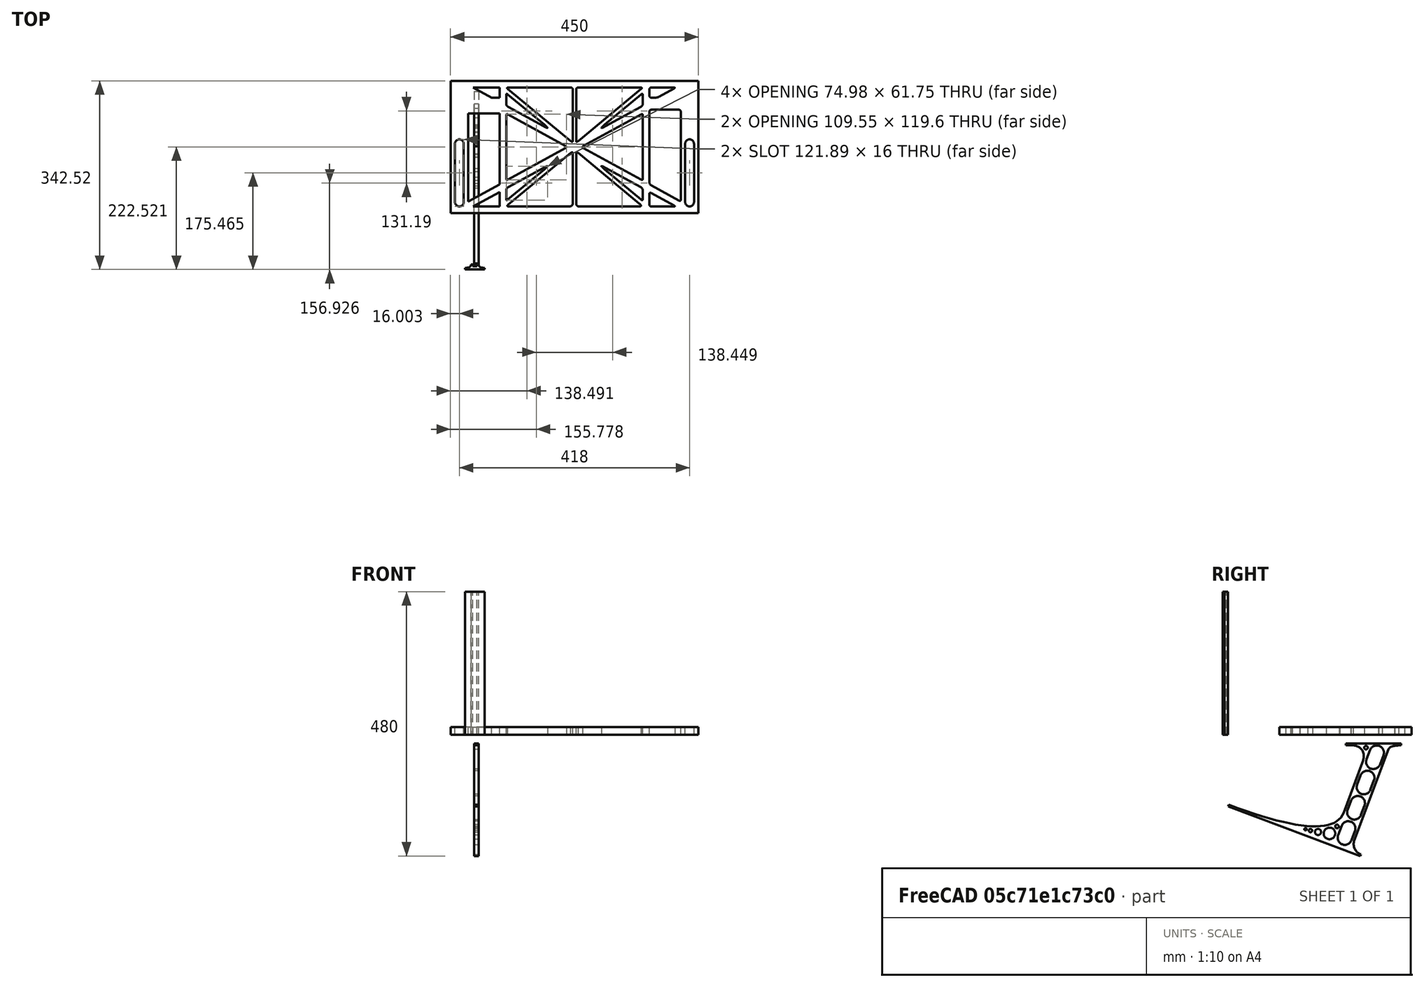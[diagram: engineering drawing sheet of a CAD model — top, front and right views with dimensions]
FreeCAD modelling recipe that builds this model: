
FCSTD DOCUMENT  (FreeCAD 0.19R0.19.2)
Label: laptopStand114
License: All rights reserved
LicenseURL: http://en.wikipedia.org/wiki/All_rights_reserved
objects: Sketcher::SketchObject×3, Part::Extrusion×3
note: 6 computed .brp shape members not serialized (recipe doc carries the construction recipe); baked Part::Feature solids carry a one-line shape summary decoded from their .brp

FEATURE [Sketcher::SketchObject] Sketch
  FullyConstrained = false
  sketch-geometry (318):
    g0: LineSegment StartX=-10.9272 StartY=-82.7794 StartZ=0 EndX=46.0728 EndY=-51.4823 EndZ=0
    g1: LineSegment StartX=-10.9272 StartY=77.3346 StartZ=0 EndX=-10.9272 EndY=-82.7794 EndZ=0
    g2: LineSegment StartX=-1.92719 StartY=-91.7794 StartZ=0 EndX=46.0728 EndY=-91.7794 EndZ=0
    g3: LineSegment StartX=46.0728 StartY=-65.424 StartZ=0 EndX=-1.92719 EndY=-91.7794 EndZ=0
    g4: LineSegment StartX=46.0728 StartY=-65.424 StartZ=0 EndX=46.0728 EndY=-91.7794 EndZ=0
    g5: LineSegment StartX=46.0728 StartY=77.3346 StartZ=0 EndX=46.0728 EndY=-51.4823 EndZ=0
    g6: LineSegment StartX=-42.9272 StartY=136.221 StartZ=0 EndX=-42.9272 EndY=-103.779 EndZ=0
    g7: LineSegment StartX=407.073 StartY=136.221 StartZ=0 EndX=407.073 EndY=-103.779 EndZ=0
    g8: ArcOfCircle CenterX=-26.9272 CenterY=22.1087 CenterZ=0 NormalX=0 NormalY=0 NormalZ=1 AngleXU=0 Radius=8 StartAngle=1e-16 EndAngle=3.14159
    g9: ArcOfCircle CenterX=-26.9272 CenterY=-83.7794 CenterZ=0 NormalX=0 NormalY=0 NormalZ=1 AngleXU=0 Radius=8 StartAngle=3.14159 EndAngle=6.28319
    g10: LineSegment StartX=-34.9272 StartY=22.1087 StartZ=0 EndX=-34.9272 EndY=-83.7794 EndZ=0
    g11: LineSegment StartX=-18.9272 StartY=22.1087 StartZ=0 EndX=-18.9272 EndY=-83.7794 EndZ=0
    g12: ArcOfCircle CenterX=391.073 CenterY=22.1087 CenterZ=0 NormalX=0 NormalY=0 NormalZ=1 AngleXU=0 Radius=8 StartAngle=-4.4e-15 EndAngle=3.14159
    g13: LineSegment StartX=399.073 StartY=22.1087 StartZ=0 EndX=399.073 EndY=-83.7794 EndZ=0
    g14: LineSegment StartX=383.073 StartY=22.1087 StartZ=0 EndX=383.073 EndY=-83.7794 EndZ=0
    g15: ArcOfCircle CenterX=391.073 CenterY=-83.7794 CenterZ=0 NormalX=0 NormalY=0 NormalZ=1 AngleXU=0 Radius=8 StartAngle=3.14159 EndAngle=6.28319
    g16: Circle CenterX=175.022 CenterY=27.0628 CenterZ=0 NormalX=0 NormalY=0 NormalZ=1 AngleXU=0 Radius=1
    g17: Circle CenterX=179.022 CenterY=24.8665 CenterZ=0 NormalX=0 NormalY=0 NormalZ=1 AngleXU=0 Radius=1
    g18: Circle CenterX=179.022 CenterY=27.0628 CenterZ=0 NormalX=0 NormalY=0 NormalZ=1 AngleXU=0 Radius=1
    g19: BSplineCurve PolesCount=3 KnotsCount=2 Degree=2 IsPeriodic=0
    g20: GeomPoint X=175.022 Y=27.0628 Z=0
    g21: GeomPoint X=179.022 Y=27.0628 Z=0
    g22: Circle CenterX=189.124 CenterY=27.0628 CenterZ=0 NormalX=0 NormalY=0 NormalZ=1 AngleXU=0 Radius=1
    g23: Circle CenterX=185.124 CenterY=24.8665 CenterZ=0 NormalX=0 NormalY=0 NormalZ=1 AngleXU=0 Radius=1
    g24: Circle CenterX=185.124 CenterY=27.0628 CenterZ=0 NormalX=0 NormalY=0 NormalZ=1 AngleXU=0 Radius=1
    g25: BSplineCurve PolesCount=3 KnotsCount=2 Degree=2 IsPeriodic=0
    g26: GeomPoint X=189.124 Y=27.0628 Z=0
    g27: GeomPoint X=185.124 Y=27.0628 Z=0
    g28: Circle CenterX=175.022 CenterY=5.37834 CenterZ=0 NormalX=0 NormalY=0 NormalZ=1 AngleXU=0 Radius=1
    g29: Circle CenterX=179.022 CenterY=7.57463 CenterZ=0 NormalX=0 NormalY=0 NormalZ=1 AngleXU=0 Radius=1
    g30: Circle CenterX=179.022 CenterY=5.34704 CenterZ=0 NormalX=0 NormalY=0 NormalZ=1 AngleXU=0 Radius=1
    g31: BSplineCurve PolesCount=3 KnotsCount=2 Degree=2 IsPeriodic=0
    g32: GeomPoint X=175.022 Y=5.37834 Z=0
    g33: GeomPoint X=179.022 Y=5.34704 Z=0
    g34: Circle CenterX=189.124 CenterY=5.37834 CenterZ=0 NormalX=0 NormalY=0 NormalZ=1 AngleXU=0 Radius=1
    g35: Circle CenterX=185.124 CenterY=7.57463 CenterZ=0 NormalX=0 NormalY=0 NormalZ=1 AngleXU=0 Radius=1
    g36: Circle CenterX=185.124 CenterY=5.34704 CenterZ=0 NormalX=0 NormalY=0 NormalZ=1 AngleXU=0 Radius=1
    g37: BSplineCurve PolesCount=3 KnotsCount=2 Degree=2 IsPeriodic=0
    g38: GeomPoint X=189.124 Y=5.37834 Z=0
    g39: GeomPoint X=185.124 Y=5.34704 Z=0
    g40: Circle CenterX=165.871 CenterY=18.1458 CenterZ=0 NormalX=0 NormalY=0 NormalZ=1 AngleXU=0 Radius=1
    g41: Circle CenterX=169.377 CenterY=16.2206 CenterZ=0 NormalX=0 NormalY=0 NormalZ=1 AngleXU=0 Radius=1
    g42: Circle CenterX=165.871 CenterY=14.2954 CenterZ=0 NormalX=0 NormalY=0 NormalZ=1 AngleXU=0 Radius=1
    g43: BSplineCurve PolesCount=3 KnotsCount=2 Degree=2 IsPeriodic=0
    g44: GeomPoint X=165.871 Y=18.1458 Z=0
    g45: GeomPoint X=165.871 Y=14.2954 Z=0
    g46: Circle CenterX=198.275 CenterY=18.1458 CenterZ=0 NormalX=0 NormalY=0 NormalZ=1 AngleXU=0 Radius=1
    g47: Circle CenterX=194.768 CenterY=16.2206 CenterZ=0 NormalX=0 NormalY=0 NormalZ=1 AngleXU=0 Radius=1
    g48: Circle CenterX=198.275 CenterY=14.2954 CenterZ=0 NormalX=0 NormalY=0 NormalZ=1 AngleXU=0 Radius=1
    g49: BSplineCurve PolesCount=3 KnotsCount=2 Degree=2 IsPeriodic=0
    g50: GeomPoint X=198.275 Y=18.1458 Z=0
    g51: GeomPoint X=198.275 Y=14.2954 Z=0
    g52: LineSegment StartX=407.073 StartY=-103.779 StartZ=0 EndX=-42.9272 EndY=-103.779 EndZ=0
    g53: LineSegment StartX=407.073 StartY=136.221 StartZ=0 EndX=-42.9272 EndY=136.221 EndZ=0
    g54: LineSegment StartX=46.0728 StartY=77.3346 StartZ=0 EndX=-10.9272 EndY=77.3346 EndZ=0
    g55: LineSegment StartX=46.0728 StartY=105.865 StartZ=0 EndX=31.5028 EndY=105.865 EndZ=0
    g56: LineSegment StartX=46.0728 StartY=124.221 StartZ=0 EndX=46.0728 EndY=105.865 EndZ=0
    g57: LineSegment StartX=-1.92719 StartY=124.221 StartZ=0 EndX=31.5028 EndY=105.865 EndZ=0
    g58: LineSegment StartX=46.0728 StartY=124.221 StartZ=0 EndX=-1.92719 EndY=124.221 EndZ=0
    g59: Circle CenterX=125.607 CenterY=54.1951 CenterZ=0 NormalX=0 NormalY=0 NormalZ=1 AngleXU=0 Radius=1
    g60: Circle CenterX=139.632 CenterY=46.4944 CenterZ=0 NormalX=0 NormalY=0 NormalZ=1 AngleXU=0 Radius=1
    g61: Circle CenterX=127.326 CenterY=56.7187 CenterZ=0 NormalX=0 NormalY=0 NormalZ=1 AngleXU=0 Radius=1
    g62: BSplineCurve PolesCount=3 KnotsCount=2 Degree=2 IsPeriodic=0
    g63: GeomPoint X=125.607 Y=54.1951 Z=0
    g64: GeomPoint X=127.326 Y=56.7187 Z=0
    g65: Circle CenterX=236.821 CenterY=56.7187 CenterZ=0 NormalX=0 NormalY=0 NormalZ=1 AngleXU=0 Radius=1
    g66: Circle CenterX=224.513 CenterY=46.4944 CenterZ=0 NormalX=0 NormalY=0 NormalZ=1 AngleXU=0 Radius=1
    g67: Circle CenterX=238.538 CenterY=54.1951 CenterZ=0 NormalX=0 NormalY=0 NormalZ=1 AngleXU=0 Radius=1
    g68: BSplineCurve PolesCount=3 KnotsCount=2 Degree=2 IsPeriodic=0
    g69: GeomPoint X=236.821 Y=56.7187 Z=0
    g70: GeomPoint X=238.538 Y=54.1951 Z=0
    g71: Circle CenterX=238.538 CenterY=-21.7539 CenterZ=0 NormalX=0 NormalY=0 NormalZ=1 AngleXU=0 Radius=1
    g72: Circle CenterX=224.513 CenterY=-14.0532 CenterZ=0 NormalX=0 NormalY=0 NormalZ=1 AngleXU=0 Radius=1
    g73: Circle CenterX=236.821 CenterY=-24.2775 CenterZ=0 NormalX=0 NormalY=0 NormalZ=1 AngleXU=0 Radius=1
    g74: BSplineCurve PolesCount=3 KnotsCount=2 Degree=2 IsPeriodic=0
    g75: GeomPoint X=238.538 Y=-21.7539 Z=0
    g76: GeomPoint X=236.821 Y=-24.2775 Z=0
    g77: Circle CenterX=125.607 CenterY=-21.7539 CenterZ=0 NormalX=0 NormalY=0 NormalZ=1 AngleXU=0 Radius=1
    g78: Circle CenterX=139.632 CenterY=-14.0532 CenterZ=0 NormalX=0 NormalY=0 NormalZ=1 AngleXU=0 Radius=1
    g79: Circle CenterX=127.325 CenterY=-24.2775 CenterZ=0 NormalX=0 NormalY=0 NormalZ=1 AngleXU=0 Radius=1
    g80: BSplineCurve PolesCount=3 KnotsCount=2 Degree=2 IsPeriodic=0
    g81: GeomPoint X=125.607 Y=-21.7539 Z=0
    g82: GeomPoint X=127.325 Y=-24.2775 Z=0
    g83: Circle CenterX=302.996 CenterY=111.695 CenterZ=0 NormalX=0 NormalY=0 NormalZ=1 AngleXU=0 Radius=1
    g84: Circle CenterX=306.073 CenterY=114.251 CenterZ=0 NormalX=0 NormalY=0 NormalZ=1 AngleXU=0 Radius=1
    g85: Circle CenterX=306.073 CenterY=110.251 CenterZ=0 NormalX=0 NormalY=0 NormalZ=1 AngleXU=0 Radius=1
    g86: BSplineCurve PolesCount=3 KnotsCount=2 Degree=2 IsPeriodic=0
    g87: GeomPoint X=302.996 Y=111.695 Z=0
    g88: GeomPoint X=306.073 Y=110.251 Z=0
    g89: Circle CenterX=306.073 CenterY=95.2763 CenterZ=0 NormalX=0 NormalY=0 NormalZ=1 AngleXU=0 Radius=1
    g90: Circle CenterX=306.073 CenterY=91.2763 CenterZ=0 NormalX=0 NormalY=0 NormalZ=1 AngleXU=0 Radius=1
    g91: Circle CenterX=302.567 CenterY=89.3511 CenterZ=0 NormalX=0 NormalY=0 NormalZ=1 AngleXU=0 Radius=1
    g92: BSplineCurve PolesCount=3 KnotsCount=2 Degree=2 IsPeriodic=0
    g93: GeomPoint X=306.073 Y=95.2763 Z=0
    g94: GeomPoint X=302.567 Y=89.3511 Z=0
    g95: LineSegment StartX=306.073 StartY=110.251 StartZ=0 EndX=306.073 EndY=95.2763 EndZ=0
    g96: LineSegment StartX=302.996 StartY=111.695 StartZ=0 EndX=236.821 EndY=56.7187 EndZ=0
    g97: LineSegment StartX=238.538 StartY=54.1951 StartZ=0 EndX=302.567 EndY=89.3511 EndZ=0
    g98: Circle CenterX=61.1496 CenterY=111.695 CenterZ=0 NormalX=0 NormalY=0 NormalZ=1 AngleXU=0 Radius=1
    g99: Circle CenterX=58.0728 CenterY=114.251 CenterZ=0 NormalX=0 NormalY=0 NormalZ=1 AngleXU=0 Radius=1
    g100: Circle CenterX=58.0728 CenterY=110.251 CenterZ=0 NormalX=0 NormalY=0 NormalZ=1 AngleXU=0 Radius=1
    g101: BSplineCurve PolesCount=3 KnotsCount=2 Degree=2 IsPeriodic=0
    g102: GeomPoint X=61.1496 Y=111.695 Z=0
    g103: GeomPoint X=58.0728 Y=110.251 Z=0
    g104: Circle CenterX=61.5791 CenterY=89.3511 CenterZ=0 NormalX=0 NormalY=0 NormalZ=1 AngleXU=0 Radius=1
    g105: Circle CenterX=58.0728 CenterY=91.2763 CenterZ=0 NormalX=0 NormalY=0 NormalZ=1 AngleXU=0 Radius=1
    g106: Circle CenterX=58.0728 CenterY=95.2763 CenterZ=0 NormalX=0 NormalY=0 NormalZ=1 AngleXU=0 Radius=1
    g107: BSplineCurve PolesCount=3 KnotsCount=2 Degree=2 IsPeriodic=0
    g108: GeomPoint X=61.5791 Y=89.3511 Z=0
    g109: GeomPoint X=58.0728 Y=95.2763 Z=0
    g110: LineSegment StartX=58.0728 StartY=110.251 StartZ=0 EndX=58.0728 EndY=95.2763 EndZ=0
    g111: LineSegment StartX=61.1496 StartY=111.695 StartZ=0 EndX=127.326 EndY=56.7187 EndZ=0
    g112: LineSegment StartX=125.607 StartY=54.1951 StartZ=0 EndX=61.5791 EndY=89.3511 EndZ=0
    g113: Circle CenterX=61.5791 CenterY=-56.9099 CenterZ=0 NormalX=0 NormalY=0 NormalZ=1 AngleXU=0 Radius=1
    g114: Circle CenterX=58.0728 CenterY=-58.8351 CenterZ=0 NormalX=0 NormalY=0 NormalZ=1 AngleXU=0 Radius=1
    g115: Circle CenterX=58.0728 CenterY=-62.8351 CenterZ=0 NormalX=0 NormalY=0 NormalZ=1 AngleXU=0 Radius=1
    g116: BSplineCurve PolesCount=3 KnotsCount=2 Degree=2 IsPeriodic=0
    g117: GeomPoint X=61.5791 Y=-56.9099 Z=0
    g118: GeomPoint X=58.0728 Y=-62.8351 Z=0
    g119: Circle CenterX=58.0728 CenterY=-77.8102 CenterZ=0 NormalX=0 NormalY=0 NormalZ=1 AngleXU=0 Radius=1
    g120: Circle CenterX=58.0728 CenterY=-81.8102 CenterZ=0 NormalX=0 NormalY=0 NormalZ=1 AngleXU=0 Radius=1
    g121: Circle CenterX=61.1496 CenterY=-79.2541 CenterZ=0 NormalX=0 NormalY=0 NormalZ=1 AngleXU=0 Radius=1
    g122: BSplineCurve PolesCount=3 KnotsCount=2 Degree=2 IsPeriodic=0
    g123: GeomPoint X=58.0728 Y=-77.8102 Z=0
    g124: GeomPoint X=61.1496 Y=-79.2541 Z=0
    g125: LineSegment StartX=58.0728 StartY=-62.8351 StartZ=0 EndX=58.0728 EndY=-77.8102 EndZ=0
    g126: LineSegment StartX=61.1496 StartY=-79.2541 StartZ=0 EndX=127.325 EndY=-24.2775 EndZ=0
    g127: LineSegment StartX=125.607 StartY=-21.7539 StartZ=0 EndX=61.5791 EndY=-56.9099 EndZ=0
    g128: Circle CenterX=302.567 CenterY=-56.9099 CenterZ=0 NormalX=0 NormalY=0 NormalZ=1 AngleXU=0 Radius=1
    g129: Circle CenterX=306.073 CenterY=-58.8351 CenterZ=0 NormalX=0 NormalY=0 NormalZ=1 AngleXU=0 Radius=1
    g130: Circle CenterX=306.073 CenterY=-62.8351 CenterZ=0 NormalX=0 NormalY=0 NormalZ=1 AngleXU=0 Radius=1
    g131: BSplineCurve PolesCount=3 KnotsCount=2 Degree=2 IsPeriodic=0
    g132: GeomPoint X=302.567 Y=-56.9099 Z=0
    g133: GeomPoint X=306.073 Y=-62.8351 Z=0
    g134: Circle CenterX=302.996 CenterY=-79.2541 CenterZ=0 NormalX=0 NormalY=0 NormalZ=1 AngleXU=0 Radius=1
    g135: Circle CenterX=306.073 CenterY=-81.8102 CenterZ=0 NormalX=0 NormalY=0 NormalZ=1 AngleXU=0 Radius=1
    g136: Circle CenterX=306.073 CenterY=-77.8102 CenterZ=0 NormalX=0 NormalY=0 NormalZ=1 AngleXU=0 Radius=1
    g137: BSplineCurve PolesCount=3 KnotsCount=2 Degree=2 IsPeriodic=0
    g138: GeomPoint X=302.996 Y=-79.2541 Z=0
    g139: GeomPoint X=306.073 Y=-77.8102 Z=0
    g140: LineSegment StartX=306.073 StartY=-62.8351 StartZ=0 EndX=306.073 EndY=-77.8102 EndZ=0
    g141: LineSegment StartX=302.996 StartY=-79.2541 StartZ=0 EndX=236.821 EndY=-24.2775 EndZ=0
    g142: LineSegment StartX=238.538 StartY=-21.7539 StartZ=0 EndX=302.567 EndY=-56.9099 EndZ=0
    g143: Circle CenterX=61.6457 CenterY=-88.8112 CenterZ=0 NormalX=0 NormalY=0 NormalZ=1 AngleXU=0 Radius=1
    g144: Circle CenterX=58.0728 CenterY=-91.7794 CenterZ=0 NormalX=0 NormalY=0 NormalZ=1 AngleXU=0 Radius=1
    g145: Circle CenterX=63.9135 CenterY=-91.7794 CenterZ=0 NormalX=0 NormalY=0 NormalZ=1 AngleXU=0 Radius=1
    g146: BSplineCurve PolesCount=3 KnotsCount=2 Degree=2 IsPeriodic=0
    g147: GeomPoint X=61.6457 Y=-88.8112 Z=0
    g148: GeomPoint X=63.9135 Y=-91.7794 Z=0
    g149: Circle CenterX=179.022 CenterY=-85.8163 CenterZ=0 NormalX=0 NormalY=0 NormalZ=1 AngleXU=0 Radius=1
    g150: Circle CenterX=179.022 CenterY=-91.7794 CenterZ=0 NormalX=0 NormalY=0 NormalZ=1 AngleXU=0 Radius=1
    g151: Circle CenterX=171.895 CenterY=-91.7794 CenterZ=0 NormalX=0 NormalY=0 NormalZ=1 AngleXU=0 Radius=1
    g152: BSplineCurve PolesCount=3 KnotsCount=2 Degree=2 IsPeriodic=0
    g153: GeomPoint X=179.022 Y=-85.8163 Z=0
    g154: GeomPoint X=171.895 Y=-91.7794 Z=0
    g155: Circle CenterX=185.124 CenterY=-86.2028 CenterZ=0 NormalX=0 NormalY=0 NormalZ=1 AngleXU=0 Radius=1
    g156: Circle CenterX=185.124 CenterY=-91.7794 CenterZ=0 NormalX=0 NormalY=0 NormalZ=1 AngleXU=0 Radius=1
    g157: Circle CenterX=191.747 CenterY=-91.7794 CenterZ=0 NormalX=0 NormalY=0 NormalZ=1 AngleXU=0 Radius=1
    g158: BSplineCurve PolesCount=3 KnotsCount=2 Degree=2 IsPeriodic=0
    g159: GeomPoint X=185.124 Y=-86.2028 Z=0
    g160: GeomPoint X=191.747 Y=-91.7794 Z=0
    g161: Circle CenterX=299.888 CenterY=-86.6413 CenterZ=0 NormalX=0 NormalY=0 NormalZ=1 AngleXU=0 Radius=1
    g162: Circle CenterX=306.073 CenterY=-91.7794 CenterZ=0 NormalX=0 NormalY=0 NormalZ=1 AngleXU=0 Radius=1
    g163: Circle CenterX=298.776 CenterY=-91.7794 CenterZ=0 NormalX=0 NormalY=0 NormalZ=1 AngleXU=0 Radius=1
    g164: BSplineCurve PolesCount=3 KnotsCount=2 Degree=2 IsPeriodic=0
    g165: GeomPoint X=299.888 Y=-86.6413 Z=0
    g166: GeomPoint X=298.776 Y=-91.7794 Z=0
    g167: LineSegment StartX=189.124 StartY=5.37834 StartZ=0 EndX=299.888 EndY=-86.6413 EndZ=0
    g168: LineSegment StartX=298.776 StartY=-91.7794 StartZ=0 EndX=191.747 EndY=-91.7794 EndZ=0
    g169: LineSegment StartX=185.124 StartY=-86.2028 StartZ=0 EndX=185.124 EndY=5.34704 EndZ=0
    g170: LineSegment StartX=179.022 StartY=5.34704 StartZ=0 EndX=179.022 EndY=-85.8163 EndZ=0
    g171: LineSegment StartX=171.895 StartY=-91.7794 StartZ=0 EndX=63.9135 EndY=-91.7794 EndZ=0
    g172: LineSegment StartX=61.6457 StartY=-88.8112 StartZ=0 EndX=175.022 EndY=5.37834 EndZ=0
    g173: Circle CenterX=302.073 CenterY=124.221 CenterZ=0 NormalX=0 NormalY=0 NormalZ=1 AngleXU=0 Radius=1
    g174: Circle CenterX=306.073 CenterY=124.221 CenterZ=0 NormalX=0 NormalY=0 NormalZ=1 AngleXU=0 Radius=1
    g175: Circle CenterX=302.996 CenterY=121.665 CenterZ=0 NormalX=0 NormalY=0 NormalZ=1 AngleXU=0 Radius=1
    g176: BSplineCurve PolesCount=3 KnotsCount=2 Degree=2 IsPeriodic=0
    g177: GeomPoint X=302.073 Y=124.221 Z=0
    g178: GeomPoint X=302.996 Y=121.665 Z=0
    g179: Circle CenterX=189.124 CenterY=124.221 CenterZ=0 NormalX=0 NormalY=0 NormalZ=1 AngleXU=0 Radius=1
    g180: Circle CenterX=185.124 CenterY=124.221 CenterZ=0 NormalX=0 NormalY=0 NormalZ=1 AngleXU=0 Radius=1
    g181: Circle CenterX=185.124 CenterY=120.221 CenterZ=0 NormalX=0 NormalY=0 NormalZ=1 AngleXU=0 Radius=1
    g182: BSplineCurve PolesCount=3 KnotsCount=2 Degree=2 IsPeriodic=0
    g183: GeomPoint X=189.124 Y=124.221 Z=0
    g184: GeomPoint X=185.124 Y=120.221 Z=0
    g185: Circle CenterX=175.022 CenterY=124.221 CenterZ=0 NormalX=0 NormalY=0 NormalZ=1 AngleXU=0 Radius=1
    g186: Circle CenterX=179.022 CenterY=124.221 CenterZ=0 NormalX=0 NormalY=0 NormalZ=1 AngleXU=0 Radius=1
    g187: Circle CenterX=179.022 CenterY=120.221 CenterZ=0 NormalX=0 NormalY=0 NormalZ=1 AngleXU=0 Radius=1
    g188: BSplineCurve PolesCount=3 KnotsCount=2 Degree=2 IsPeriodic=0
    g189: GeomPoint X=175.022 Y=124.221 Z=0
    g190: GeomPoint X=179.022 Y=120.221 Z=0
    g191: Circle CenterX=62.0728 CenterY=124.221 CenterZ=0 NormalX=0 NormalY=0 NormalZ=1 AngleXU=0 Radius=1
    g192: Circle CenterX=58.0728 CenterY=124.221 CenterZ=0 NormalX=0 NormalY=0 NormalZ=1 AngleXU=0 Radius=1
    g193: Circle CenterX=61.1496 CenterY=121.665 CenterZ=0 NormalX=0 NormalY=0 NormalZ=1 AngleXU=0 Radius=1
    g194: BSplineCurve PolesCount=3 KnotsCount=2 Degree=2 IsPeriodic=0
    g195: GeomPoint X=62.0728 Y=124.221 Z=0
    g196: GeomPoint X=61.1496 Y=121.665 Z=0
    g197: LineSegment StartX=62.0728 StartY=124.221 StartZ=0 EndX=175.022 EndY=124.221 EndZ=0
    g198: LineSegment StartX=179.022 StartY=120.221 StartZ=0 EndX=179.022 EndY=27.0628 EndZ=0
    g199: LineSegment StartX=185.124 StartY=27.0628 StartZ=0 EndX=185.124 EndY=120.221 EndZ=0
    g200: LineSegment StartX=189.124 StartY=124.221 StartZ=0 EndX=302.073 EndY=124.221 EndZ=0
    g201: LineSegment StartX=302.996 StartY=121.665 StartZ=0 EndX=189.124 EndY=27.0628 EndZ=0
    g202: LineSegment StartX=175.022 StartY=27.0628 StartZ=0 EndX=61.1496 EndY=121.665 EndZ=0
    g203: Circle CenterX=61.5791 CenterY=75.4095 CenterZ=0 NormalX=0 NormalY=0 NormalZ=1 AngleXU=0 Radius=1
    g204: Circle CenterX=58.0728 CenterY=77.3346 CenterZ=0 NormalX=0 NormalY=0 NormalZ=1 AngleXU=0 Radius=1
    g205: Circle CenterX=58.0728 CenterY=73.3346 CenterZ=0 NormalX=0 NormalY=0 NormalZ=1 AngleXU=0 Radius=1
    g206: BSplineCurve PolesCount=3 KnotsCount=2 Degree=2 IsPeriodic=0
    g207: GeomPoint X=61.5791 Y=75.4095 Z=0
    g208: GeomPoint X=58.0728 Y=73.3346 Z=0
    g209: Circle CenterX=58.0728 CenterY=-40.8935 CenterZ=0 NormalX=0 NormalY=0 NormalZ=1 AngleXU=0 Radius=1
    g210: Circle CenterX=58.0728 CenterY=-44.8935 CenterZ=0 NormalX=0 NormalY=0 NormalZ=1 AngleXU=0 Radius=1
    g211: Circle CenterX=61.5791 CenterY=-42.9683 CenterZ=0 NormalX=0 NormalY=0 NormalZ=1 AngleXU=0 Radius=1
    g212: BSplineCurve PolesCount=3 KnotsCount=2 Degree=2 IsPeriodic=0
    g213: GeomPoint X=58.0728 Y=-40.8935 Z=0
    g214: GeomPoint X=61.5791 Y=-42.9683 Z=0
    g215: LineSegment StartX=61.5791 StartY=-42.9683 StartZ=0 EndX=165.871 EndY=14.2954 EndZ=0
    g216: LineSegment StartX=165.871 StartY=18.1458 StartZ=0 EndX=61.5791 EndY=75.4095 EndZ=0
    g217: LineSegment StartX=58.0728 StartY=73.3346 StartZ=0 EndX=58.0728 EndY=-40.8935 EndZ=0
    g218: Circle CenterX=302.567 CenterY=-42.9683 CenterZ=0 NormalX=0 NormalY=0 NormalZ=1 AngleXU=0 Radius=1
    g219: Circle CenterX=306.073 CenterY=-44.8935 CenterZ=0 NormalX=0 NormalY=0 NormalZ=1 AngleXU=0 Radius=1
    g220: Circle CenterX=306.073 CenterY=-40.8935 CenterZ=0 NormalX=0 NormalY=0 NormalZ=1 AngleXU=0 Radius=1
    g221: BSplineCurve PolesCount=3 KnotsCount=2 Degree=2 IsPeriodic=0
    g222: GeomPoint X=302.567 Y=-42.9683 Z=0
    g223: GeomPoint X=306.073 Y=-40.8935 Z=0
    g224: Circle CenterX=306.073 CenterY=73.3346 CenterZ=0 NormalX=0 NormalY=0 NormalZ=1 AngleXU=0 Radius=1
    g225: Circle CenterX=306.073 CenterY=77.3346 CenterZ=0 NormalX=0 NormalY=0 NormalZ=1 AngleXU=0 Radius=1
    g226: Circle CenterX=302.567 CenterY=75.4095 CenterZ=0 NormalX=0 NormalY=0 NormalZ=1 AngleXU=0 Radius=1
    g227: BSplineCurve PolesCount=3 KnotsCount=2 Degree=2 IsPeriodic=0
    g228: GeomPoint X=306.073 Y=73.3346 Z=0
    g229: GeomPoint X=302.567 Y=75.4095 Z=0
    g230: LineSegment StartX=302.567 StartY=-42.9683 StartZ=0 EndX=198.275 EndY=14.2954 EndZ=0
    g231: LineSegment StartX=198.275 StartY=18.1458 StartZ=0 EndX=302.567 EndY=75.4095 EndZ=0
    g232: LineSegment StartX=306.073 StartY=73.3346 StartZ=0 EndX=306.073 EndY=-40.8935 EndZ=0
    g233: LineSegment StartX=322.073 StartY=105.865 StartZ=0 EndX=328.643 EndY=105.865 EndZ=0
    g234: LineSegment StartX=318.073 StartY=120.221 StartZ=0 EndX=318.073 EndY=109.865 EndZ=0
    g235: LineSegment StartX=336.157 StartY=107.779 StartZ=0 EndX=362.567 EndY=122.294 EndZ=0
    g236: Circle CenterX=362.073 CenterY=124.221 CenterZ=0 NormalX=0 NormalY=0 NormalZ=1 AngleXU=0 Radius=1
    g237: Circle CenterX=366.073 CenterY=124.221 CenterZ=0 NormalX=0 NormalY=0 NormalZ=1 AngleXU=0 Radius=1
    g238: Circle CenterX=362.567 CenterY=122.294 CenterZ=0 NormalX=0 NormalY=0 NormalZ=1 AngleXU=0 Radius=1
    g239: BSplineCurve PolesCount=3 KnotsCount=2 Degree=2 IsPeriodic=0
    g240: GeomPoint X=362.073 Y=124.221 Z=0
    g241: GeomPoint X=362.567 Y=122.294 Z=0
    g242: Circle CenterX=322.073 CenterY=124.221 CenterZ=0 NormalX=0 NormalY=0 NormalZ=1 AngleXU=0 Radius=1
    g243: Circle CenterX=318.073 CenterY=124.221 CenterZ=0 NormalX=0 NormalY=0 NormalZ=1 AngleXU=0 Radius=1
    g244: Circle CenterX=318.073 CenterY=120.221 CenterZ=0 NormalX=0 NormalY=0 NormalZ=1 AngleXU=0 Radius=1
    g245: BSplineCurve PolesCount=3 KnotsCount=2 Degree=2 IsPeriodic=0
    g246: GeomPoint X=322.073 Y=124.221 Z=0
    g247: GeomPoint X=318.073 Y=120.221 Z=0
    g248: Circle CenterX=322.073 CenterY=105.865 CenterZ=0 NormalX=0 NormalY=0 NormalZ=1 AngleXU=0 Radius=1
    g249: Circle CenterX=318.073 CenterY=105.865 CenterZ=0 NormalX=0 NormalY=0 NormalZ=1 AngleXU=0 Radius=1
    g250: Circle CenterX=318.073 CenterY=109.865 CenterZ=0 NormalX=0 NormalY=0 NormalZ=1 AngleXU=0 Radius=1
    g251: BSplineCurve PolesCount=3 KnotsCount=2 Degree=2 IsPeriodic=0
    g252: GeomPoint X=322.073 Y=105.865 Z=0
    g253: GeomPoint X=318.073 Y=109.865 Z=0
    g254: Circle CenterX=336.157 CenterY=107.779 CenterZ=0 NormalX=0 NormalY=0 NormalZ=1 AngleXU=0 Radius=1
    g255: Circle CenterX=332.651 CenterY=105.853 CenterZ=0 NormalX=0 NormalY=0 NormalZ=1 AngleXU=0 Radius=1
    g256: Circle CenterX=328.643 CenterY=105.865 CenterZ=0 NormalX=0 NormalY=0 NormalZ=1 AngleXU=0 Radius=1
    g257: BSplineCurve PolesCount=3 KnotsCount=2 Degree=2 IsPeriodic=0
    g258: GeomPoint X=336.157 Y=107.779 Z=0
    g259: GeomPoint X=328.643 Y=105.865 Z=0
    g260: LineSegment StartX=322.073 StartY=124.221 StartZ=0 EndX=362.073 EndY=124.221 EndZ=0
    g261: Circle CenterX=371.567 CenterY=-80.8644 CenterZ=0 NormalX=0 NormalY=0 NormalZ=1 AngleXU=0 Radius=1
    g262: Circle CenterX=375.073 CenterY=-82.7896 CenterZ=0 NormalX=0 NormalY=0 NormalZ=1 AngleXU=0 Radius=1
    g263: Circle CenterX=375.073 CenterY=-78.7896 CenterZ=0 NormalX=0 NormalY=0 NormalZ=1 AngleXU=0 Radius=1
    g264: BSplineCurve PolesCount=3 KnotsCount=2 Degree=2 IsPeriodic=0
    g265: GeomPoint X=371.567 Y=-80.8644 Z=0
    g266: GeomPoint X=375.073 Y=-78.7896 Z=0
    g267: Circle CenterX=321.579 CenterY=-53.4075 CenterZ=0 NormalX=0 NormalY=0 NormalZ=1 AngleXU=0 Radius=1
    g268: Circle CenterX=318.073 CenterY=-51.4823 CenterZ=0 NormalX=0 NormalY=0 NormalZ=1 AngleXU=0 Radius=1
    g269: Circle CenterX=318.073 CenterY=-47.4823 CenterZ=0 NormalX=0 NormalY=0 NormalZ=1 AngleXU=0 Radius=1
    g270: BSplineCurve PolesCount=3 KnotsCount=2 Degree=2 IsPeriodic=0
    g271: GeomPoint X=321.579 Y=-53.4075 Z=0
    g272: GeomPoint X=318.073 Y=-47.4823 Z=0
    g273: Circle CenterX=318.073 CenterY=79.9235 CenterZ=0 NormalX=0 NormalY=0 NormalZ=1 AngleXU=0 Radius=1
    g274: Circle CenterX=318.073 CenterY=83.9235 CenterZ=0 NormalX=0 NormalY=0 NormalZ=1 AngleXU=0 Radius=1
    g275: Circle CenterX=322.073 CenterY=83.9235 CenterZ=0 NormalX=0 NormalY=0 NormalZ=1 AngleXU=0 Radius=1
    g276: BSplineCurve PolesCount=3 KnotsCount=2 Degree=2 IsPeriodic=0
    g277: GeomPoint X=318.073 Y=79.9235 Z=0
    g278: GeomPoint X=322.073 Y=83.9235 Z=0
    g279: Circle CenterX=375.073 CenterY=79.9235 CenterZ=0 NormalX=0 NormalY=0 NormalZ=1 AngleXU=0 Radius=1
    g280: Circle CenterX=375.073 CenterY=83.9235 CenterZ=0 NormalX=0 NormalY=0 NormalZ=1 AngleXU=0 Radius=1
    g281: Circle CenterX=371.073 CenterY=83.9235 CenterZ=0 NormalX=0 NormalY=0 NormalZ=1 AngleXU=0 Radius=1
    g282: BSplineCurve PolesCount=3 KnotsCount=2 Degree=2 IsPeriodic=0
    g283: GeomPoint X=375.073 Y=79.9235 Z=0
    g284: GeomPoint X=371.073 Y=83.9235 Z=0
    g285: LineSegment StartX=322.073 StartY=83.9235 StartZ=0 EndX=371.073 EndY=83.9235 EndZ=0
    g286: LineSegment StartX=375.073 StartY=79.9235 StartZ=0 EndX=375.073 EndY=-78.7896 EndZ=0
    g287: LineSegment StartX=371.567 StartY=-80.8644 StartZ=0 EndX=321.579 EndY=-53.4075 EndZ=0
    g288: LineSegment StartX=318.073 StartY=-47.4823 StartZ=0 EndX=318.073 EndY=79.9235 EndZ=0
    g289: Circle CenterX=321.579 CenterY=-67.3492 CenterZ=0 NormalX=0 NormalY=0 NormalZ=1 AngleXU=0 Radius=1
    g290: Circle CenterX=318.073 CenterY=-65.424 CenterZ=0 NormalX=0 NormalY=0 NormalZ=1 AngleXU=0 Radius=1
    g291: Circle CenterX=318.073 CenterY=-69.424 CenterZ=0 NormalX=0 NormalY=0 NormalZ=1 AngleXU=0 Radius=1
    g292: BSplineCurve PolesCount=3 KnotsCount=2 Degree=2 IsPeriodic=0
    g293: GeomPoint X=321.579 Y=-67.3492 Z=0
    g294: GeomPoint X=318.073 Y=-69.424 Z=0
    g295: Circle CenterX=362.567 CenterY=-89.8542 CenterZ=0 NormalX=0 NormalY=0 NormalZ=1 AngleXU=0 Radius=1
    g296: Circle CenterX=366.073 CenterY=-91.7794 CenterZ=0 NormalX=0 NormalY=0 NormalZ=1 AngleXU=0 Radius=1
    g297: Circle CenterX=362.073 CenterY=-91.7794 CenterZ=0 NormalX=0 NormalY=0 NormalZ=1 AngleXU=0 Radius=1
    g298: BSplineCurve PolesCount=3 KnotsCount=2 Degree=2 IsPeriodic=0
    g299: GeomPoint X=362.567 Y=-89.8542 Z=0
    g300: GeomPoint X=362.073 Y=-91.7794 Z=0
    g301: Circle CenterX=322.073 CenterY=-91.7794 CenterZ=0 NormalX=0 NormalY=0 NormalZ=1 AngleXU=0 Radius=1
    g302: Circle CenterX=318.073 CenterY=-91.7794 CenterZ=0 NormalX=0 NormalY=0 NormalZ=1 AngleXU=0 Radius=1
    g303: Circle CenterX=318.073 CenterY=-87.7794 CenterZ=0 NormalX=0 NormalY=0 NormalZ=1 AngleXU=0 Radius=1
    g304: BSplineCurve PolesCount=3 KnotsCount=2 Degree=2 IsPeriodic=0
    g305: GeomPoint X=322.073 Y=-91.7794 Z=0
    g306: GeomPoint X=318.073 Y=-87.7794 Z=0
    g307: LineSegment StartX=362.567 StartY=-89.8542 StartZ=0 EndX=321.579 EndY=-67.3492 EndZ=0
    g308: LineSegment StartX=318.073 StartY=-69.424 StartZ=0 EndX=318.073 EndY=-87.7794 EndZ=0
    g309: LineSegment StartX=322.073 StartY=-91.7794 StartZ=0 EndX=362.073 EndY=-91.7794 EndZ=0
    g310: LineSegment StartX=-0.23891 StartY=125.592 StartZ=0 EndX=2.49403 EndY=125.592 EndZ=0
    g311: LineSegment StartX=-0.98687 StartY=122.83 StartZ=0 EndX=1.65976 EndY=121.478 EndZ=0
    g312: LineSegment StartX=29.7658 StartY=105.483 StartZ=0 EndX=27.8959 EndY=106.461 EndZ=0
    g313: LineSegment StartX=32.7577 StartY=104.735 StartZ=0 EndX=35.4906 EndY=104.735 EndZ=0
    g314: LineSegment StartX=44.984 StartY=104.994 StartZ=0 EndX=42.625 EndY=104.994 EndZ=0
    g315: LineSegment StartX=47.084 StartY=106.548 StartZ=0 EndX=47.084 EndY=108.907 EndZ=0
    g316: LineSegment StartX=47.1703 StartY=123.204 StartZ=0 EndX=47.1703 EndY=121.334 EndZ=0
    g317: LineSegment StartX=45.3292 StartY=125.161 StartZ=0 EndX=42.9127 EndY=125.161 EndZ=0
  constraints (525):
    c: Horizontal(g2)
    c: Coincident(g4,g3)
    c: Coincident(g0,g5)
    c: Block(g4)
    c: Block(g3)
    c: Block(g0)
    c: Block(g1)
    c: Block(g2)
    c: Vertical(g6)
    c: Vertical(g7)
    c: Block(g7)
    c: Block(g6)
    c: Tangent(g8,g11) = 1.5708
    c: Tangent(g8,g10) = -1.5708
    c: Tangent(g10,g9) = -1.5708
    c: Tangent(g11,g9) = 1.5708
    c: Vertical(g10)
    c: Equal(g8,g9)
    c: Block(g11)
    c: Block(g10)
    c: Tangent(g12,g13) = 1.5708
    c: Tangent(g13,g15) = 1.5708
    c: Equal(g12,g15)
    c: Coincident(g14,g12)
    c: Coincident(g14,g15)
    c: Block(g13)
    c: Block(g14)
    c: Weight(g16) = 1
    c: Equal(g16,g17)
    c: Equal(g16,g18)
    c: InternalAlignment(g16,g19)
    c: InternalAlignment(g17,g19)
    c: InternalAlignment(g18,g19)
    c: InternalAlignment(g20,g19)
    c: InternalAlignment(g21,g19)
    c: Weight(g22) = 1
    c: Equal(g22,g23)
    c: Equal(g22,g24)
    c: InternalAlignment(g22,g25)
    c: InternalAlignment(g23,g25)
    c: InternalAlignment(g24,g25)
    c: InternalAlignment(g26,g25)
    c: InternalAlignment(g27,g25)
    c: Block(g25)
    c: Block(g19)
    c: Weight(g28) = 1
    c: Equal(g28,g29)
    c: Equal(g28,g30)
    c: InternalAlignment(g28,g31)
    c: InternalAlignment(g29,g31)
    c: InternalAlignment(g30,g31)
    c: InternalAlignment(g32,g31)
    c: InternalAlignment(g33,g31)
    c: Weight(g34) = 1
    c: Equal(g34,g35)
    c: Equal(g34,g36)
    c: InternalAlignment(g34,g37)
    c: InternalAlignment(g35,g37)
    c: InternalAlignment(g36,g37)
    c: InternalAlignment(g38,g37)
    c: InternalAlignment(g39,g37)
    c: Block(g37)
    c: Block(g31)
    c: Weight(g40) = 1
    c: Equal(g40,g41)
    c: Equal(g40,g42)
    c: InternalAlignment(g40,g43)
    c: InternalAlignment(g41,g43)
    c: InternalAlignment(g42,g43)
    c: InternalAlignment(g44,g43)
    c: InternalAlignment(g45,g43)
    c: Weight(g46) = 1
    c: Equal(g46,g47)
    c: Equal(g46,g48)
    c: InternalAlignment(g46,g49)
    c: InternalAlignment(g47,g49)
    c: InternalAlignment(g48,g49)
    c: InternalAlignment(g50,g49)
    c: InternalAlignment(g51,g49)
    c: Block(g43)
    c: Block(g49)
    c: Coincident(g52,g7)
    c: Coincident(g52,g6)
    c: Horizontal(g52)
    c: Distance(g52) = 450
    c: Coincident(g53,g7)
    c: Coincident(g53,g6)
    c: Horizontal(g53)
    c: Horizontal(g54)
    c: Coincident(g5,g54)
    c: Horizontal(g55)
    c: Vertical(g56)
    c: Block(g56)
    c: Block(g55)
    c: Block(g54)
    c: Distance(g56) = 18.3554
    c: Coincident(g58,g56)
    c: Coincident(g58,g57)
    c: Horizontal(g58)
    c: Block(g58)
    c: Block(g57)
    c: Coincident(g55,g57)
    c: Coincident(g1,g54)
    c: Weight(g59) = 1
    c: Equal(g59,g60)
    c: Equal(g59,g61)
    c: InternalAlignment(g59,g62)
    c: InternalAlignment(g60,g62)
    c: InternalAlignment(g61,g62)
    c: InternalAlignment(g63,g62)
    c: InternalAlignment(g64,g62)
    c: Block(g62)
    c: Weight(g65) = 1
    c: Equal(g65,g66)
    c: Equal(g65,g67)
    c: InternalAlignment(g65,g68)
    c: InternalAlignment(g66,g68)
    c: InternalAlignment(g67,g68)
    c: InternalAlignment(g69,g68)
    c: InternalAlignment(g70,g68)
    c: Block(g68)
    c: Weight(g71) = 1
    c: Equal(g71,g72)
    c: Equal(g71,g73)
    c: InternalAlignment(g71,g74)
    c: InternalAlignment(g72,g74)
    c: InternalAlignment(g73,g74)
    c: InternalAlignment(g75,g74)
    c: InternalAlignment(g76,g74)
    c: Block(g74)
    c: Weight(g77) = 1
    c: Equal(g77,g78)
    c: Equal(g77,g79)
    c: InternalAlignment(g77,g80)
    c: InternalAlignment(g78,g80)
    c: InternalAlignment(g79,g80)
    c: InternalAlignment(g81,g80)
    c: InternalAlignment(g82,g80)
    c: Block(g80)
    c: Weight(g83) = 1
    c: Equal(g83,g84)
    c: Equal(g83,g85)
    c: InternalAlignment(g83,g86)
    c: InternalAlignment(g84,g86)
    c: InternalAlignment(g85,g86)
    c: InternalAlignment(g87,g86)
    c: InternalAlignment(g88,g86)
    c: Weight(g89) = 1
    c: Equal(g89,g90)
    c: Equal(g89,g91)
    c: InternalAlignment(g89,g92)
    c: InternalAlignment(g90,g92)
    c: InternalAlignment(g91,g92)
    c: InternalAlignment(g93,g92)
    c: InternalAlignment(g94,g92)
    c: Block(g86)
    c: Block(g92)
    c: Coincident(g95,g86)
    c: Coincident(g95,g92)
    c: Vertical(g95)
    c: Coincident(g96,g86)
    c: Coincident(g96,g68)
    c: Coincident(g97,g68)
    c: Coincident(g97,g92)
    c: Weight(g98) = 1
    c: Equal(g98,g99)
    c: Equal(g98,g100)
    c: InternalAlignment(g98,g101)
    c: InternalAlignment(g99,g101)
    c: InternalAlignment(g100,g101)
    c: InternalAlignment(g102,g101)
    c: InternalAlignment(g103,g101)
    c: Weight(g104) = 1
    c: Equal(g104,g105)
    c: Equal(g104,g106)
    c: InternalAlignment(g104,g107)
    c: InternalAlignment(g105,g107)
    c: InternalAlignment(g106,g107)
    c: InternalAlignment(g108,g107)
    c: InternalAlignment(g109,g107)
    c: Block(g101)
    c: Block(g107)
    c: Coincident(g110,g101)
    c: Coincident(g110,g107)
    c: Vertical(g110)
    c: Coincident(g111,g101)
    c: Coincident(g111,g62)
    c: Coincident(g112,g62)
    c: Coincident(g112,g107)
    c: Weight(g113) = 1
    c: Equal(g113,g114)
    c: Equal(g113,g115)
    c: InternalAlignment(g113,g116)
    c: InternalAlignment(g114,g116)
    c: InternalAlignment(g115,g116)
    c: InternalAlignment(g117,g116)
    c: InternalAlignment(g118,g116)
    c: Weight(g119) = 1
    c: Equal(g119,g120)
    c: Equal(g119,g121)
    c: InternalAlignment(g119,g122)
    c: InternalAlignment(g120,g122)
    c: InternalAlignment(g121,g122)
    c: InternalAlignment(g123,g122)
    c: InternalAlignment(g124,g122)
    c: Block(g116)
    c: Block(g122)
    c: Coincident(g125,g116)
    c: Coincident(g125,g122)
    c: Vertical(g125)
    c: Coincident(g126,g122)
    c: Coincident(g126,g80)
    c: Coincident(g127,g80)
    c: Coincident(g127,g116)
    c: Weight(g128) = 1
    c: Equal(g128,g129)
    c: Equal(g128,g130)
    c: InternalAlignment(g128,g131)
    c: InternalAlignment(g129,g131)
    c: InternalAlignment(g130,g131)
    c: InternalAlignment(g132,g131)
    c: InternalAlignment(g133,g131)
    c: Weight(g134) = 1
    c: Equal(g134,g135)
    c: Equal(g134,g136)
    c: InternalAlignment(g134,g137)
    c: InternalAlignment(g135,g137)
    c: InternalAlignment(g136,g137)
    c: InternalAlignment(g138,g137)
    c: InternalAlignment(g139,g137)
    c: Block(g131)
    c: Block(g137)
    c: Coincident(g140,g131)
    c: Coincident(g140,g137)
    c: Vertical(g140)
    c: Coincident(g141,g137)
    c: Coincident(g141,g74)
    c: Coincident(g142,g74)
    c: Coincident(g142,g131)
    c: Weight(g143) = 1
    c: Equal(g143,g144)
    c: Equal(g143,g145)
    c: InternalAlignment(g143,g146)
    c: InternalAlignment(g144,g146)
    c: InternalAlignment(g145,g146)
    c: InternalAlignment(g147,g146)
    c: InternalAlignment(g148,g146)
    c: Weight(g149) = 1
    c: Equal(g149,g150)
    c: Equal(g149,g151)
    c: InternalAlignment(g149,g152)
    c: InternalAlignment(g150,g152)
    c: InternalAlignment(g151,g152)
    c: InternalAlignment(g153,g152)
    c: InternalAlignment(g154,g152)
    c: Weight(g155) = 1
    c: Equal(g155,g156)
    c: Equal(g155,g157)
    c: InternalAlignment(g155,g158)
    c: InternalAlignment(g156,g158)
    c: InternalAlignment(g157,g158)
    c: InternalAlignment(g159,g158)
    c: InternalAlignment(g160,g158)
    c: Weight(g161) = 1
    c: Equal(g161,g162)
    c: Equal(g161,g163)
    c: InternalAlignment(g161,g164)
    c: InternalAlignment(g162,g164)
    c: InternalAlignment(g163,g164)
    c: InternalAlignment(g165,g164)
    c: InternalAlignment(g166,g164)
    c: Block(g164)
    c: Block(g158)
    c: Block(g152)
    c: Block(g146)
    c: Coincident(g167,g37)
    c: Coincident(g167,g164)
    c: Coincident(g168,g164)
    c: Coincident(g168,g158)
    c: Horizontal(g168)
    c: Coincident(g169,g158)
    c: Coincident(g169,g37)
    c: Vertical(g169)
    c: Coincident(g170,g31)
    c: Coincident(g170,g152)
    c: Vertical(g170)
    c: Coincident(g171,g152)
    c: Coincident(g171,g146)
    c: Horizontal(g171)
    c: Coincident(g172,g146)
    c: Coincident(g172,g31)
    c: Weight(g173) = 1
    c: Equal(g173,g174)
    c: Equal(g173,g175)
    c: InternalAlignment(g173,g176)
    c: InternalAlignment(g174,g176)
    c: InternalAlignment(g175,g176)
    c: InternalAlignment(g177,g176)
    c: InternalAlignment(g178,g176)
    c: Weight(g179) = 1
    c: Equal(g179,g180)
    c: Equal(g179,g181)
    c: InternalAlignment(g179,g182)
    c: InternalAlignment(g180,g182)
    c: InternalAlignment(g181,g182)
    c: InternalAlignment(g183,g182)
    c: InternalAlignment(g184,g182)
    c: Weight(g185) = 1
    c: Equal(g185,g186)
    c: Equal(g185,g187)
    c: InternalAlignment(g185,g188)
    c: InternalAlignment(g186,g188)
    c: InternalAlignment(g187,g188)
    c: InternalAlignment(g189,g188)
    c: InternalAlignment(g190,g188)
    c: Weight(g191) = 1
    c: Equal(g191,g192)
    c: Equal(g191,g193)
    c: InternalAlignment(g191,g194)
    c: InternalAlignment(g192,g194)
    c: InternalAlignment(g193,g194)
    c: InternalAlignment(g195,g194)
    c: InternalAlignment(g196,g194)
    c: Block(g194)
    c: Block(g188)
    c: Block(g182)
    c: Block(g176)
    c: Coincident(g197,g194)
    c: Coincident(g197,g188)
    c: Horizontal(g197)
    c: Coincident(g198,g188)
    c: Coincident(g198,g19)
    c: Vertical(g198)
    c: Coincident(g199,g25)
    c: Coincident(g199,g182)
    c: Vertical(g199)
    c: Coincident(g200,g182)
    c: Coincident(g200,g176)
    c: Horizontal(g200)
    c: Coincident(g201,g176)
    c: Coincident(g201,g25)
    c: Coincident(g202,g19)
    c: Weight(g203) = 1
    c: Equal(g203,g204)
    c: Equal(g203,g205)
    c: InternalAlignment(g203,g206)
    c: InternalAlignment(g204,g206)
    c: InternalAlignment(g205,g206)
    c: InternalAlignment(g207,g206)
    c: InternalAlignment(g208,g206)
    c: Weight(g209) = 1
    c: Equal(g209,g210)
    c: Equal(g209,g211)
    c: InternalAlignment(g209,g212)
    c: InternalAlignment(g210,g212)
    c: InternalAlignment(g211,g212)
    c: InternalAlignment(g213,g212)
    c: InternalAlignment(g214,g212)
    c: Block(g212)
    c: Block(g206)
    c: Coincident(g215,g212)
    c: Coincident(g215,g43)
    c: Coincident(g216,g43)
    c: Coincident(g216,g206)
    c: Coincident(g217,g206)
    c: Coincident(g217,g212)
    c: Vertical(g217)
    c: Weight(g218) = 1
    c: Equal(g218,g219)
    c: Equal(g218,g220)
    c: InternalAlignment(g218,g221)
    c: InternalAlignment(g219,g221)
    c: InternalAlignment(g220,g221)
    c: InternalAlignment(g222,g221)
    c: InternalAlignment(g223,g221)
    c: Weight(g224) = 1
    c: Equal(g224,g225)
    c: Equal(g224,g226)
    c: InternalAlignment(g224,g227)
    c: InternalAlignment(g225,g227)
    c: InternalAlignment(g226,g227)
    c: InternalAlignment(g228,g227)
    c: InternalAlignment(g229,g227)
    c: Block(g227)
    c: Block(g221)
    c: Coincident(g230,g221)
    c: Coincident(g230,g49)
    c: Coincident(g231,g49)
    c: Coincident(g231,g227)
    c: Coincident(g232,g227)
    c: Coincident(g232,g221)
    c: Vertical(g232)
    c: Horizontal(g233)
    c: Block(g233)
    c: Vertical(g234)
    c: Block(g234)
    c: Block(g235)
    c: Weight(g236) = 1
    c: Equal(g236,g237)
    c: Equal(g236,g238)
    c: InternalAlignment(g236,g239)
    c: InternalAlignment(g237,g239)
    c: InternalAlignment(g238,g239)
    c: InternalAlignment(g240,g239)
    c: InternalAlignment(g241,g239)
    c: Weight(g242) = 1
    c: Equal(g242,g243)
    c: Equal(g242,g244)
    c: InternalAlignment(g242,g245)
    c: InternalAlignment(g243,g245)
    c: InternalAlignment(g244,g245)
    c: InternalAlignment(g246,g245)
    c: InternalAlignment(g247,g245)
    c: Weight(g248) = 1
    c: Equal(g248,g249)
    c: Equal(g248,g250)
    c: InternalAlignment(g248,g251)
    c: InternalAlignment(g249,g251)
    c: InternalAlignment(g250,g251)
    c: InternalAlignment(g252,g251)
    c: InternalAlignment(g253,g251)
    c: Weight(g254) = 1
    c: Equal(g254,g255)
    c: Equal(g254,g256)
    c: InternalAlignment(g254,g257)
    c: InternalAlignment(g255,g257)
    c: InternalAlignment(g256,g257)
    c: InternalAlignment(g258,g257)
    c: InternalAlignment(g259,g257)
    c: Block(g239)
    c: Block(g245)
    c: Block(g251)
    c: Block(g257)
    c: Coincident(g260,g245)
    c: Coincident(g260,g239)
    c: Horizontal(g260)
    c: Block(g202)
    c: Weight(g261) = 1
    c: Equal(g261,g262)
    c: Equal(g261,g263)
    c: InternalAlignment(g261,g264)
    c: InternalAlignment(g262,g264)
    c: InternalAlignment(g263,g264)
    c: InternalAlignment(g265,g264)
    c: InternalAlignment(g266,g264)
    c: Weight(g267) = 1
    c: Equal(g267,g268)
    c: Equal(g267,g269)
    c: InternalAlignment(g267,g270)
    c: InternalAlignment(g268,g270)
    c: InternalAlignment(g269,g270)
    c: InternalAlignment(g271,g270)
    c: InternalAlignment(g272,g270)
    c: Weight(g273) = 1
    c: Equal(g273,g274)
    c: Equal(g273,g275)
    c: InternalAlignment(g273,g276)
    c: InternalAlignment(g274,g276)
    c: InternalAlignment(g275,g276)
    c: InternalAlignment(g277,g276)
    c: InternalAlignment(g278,g276)
    c: Weight(g279) = 1
    c: Equal(g279,g280)
    c: Equal(g279,g281)
    c: InternalAlignment(g279,g282)
    c: InternalAlignment(g280,g282)
    c: InternalAlignment(g281,g282)
    c: InternalAlignment(g283,g282)
    c: InternalAlignment(g284,g282)
    c: Block(g264)
    c: Block(g270)
    c: Block(g276)
    c: Block(g282)
    c: Coincident(g285,g276)
    c: Coincident(g285,g282)
    c: Horizontal(g285)
    c: Coincident(g286,g282)
    c: Coincident(g286,g264)
    c: Vertical(g286)
    c: Coincident(g287,g264)
    c: Coincident(g287,g270)
    c: Coincident(g288,g270)
    c: Coincident(g288,g276)
    c: Vertical(g288)
    c: Weight(g289) = 1
    c: Equal(g289,g290)
    c: Equal(g289,g291)
    c: InternalAlignment(g289,g292)
    c: InternalAlignment(g290,g292)
    c: InternalAlignment(g291,g292)
    c: InternalAlignment(g293,g292)
    c: InternalAlignment(g294,g292)
    c: Weight(g295) = 1
    c: Equal(g295,g296)
    c: Equal(g295,g297)
    c: InternalAlignment(g295,g298)
    c: InternalAlignment(g296,g298)
    c: InternalAlignment(g297,g298)
    c: InternalAlignment(g299,g298)
    c: InternalAlignment(g300,g298)
    c: Weight(g301) = 1
    c: Equal(g301,g302)
    c: Equal(g301,g303)
    c: InternalAlignment(g301,g304)
    c: InternalAlignment(g302,g304)
    c: InternalAlignment(g303,g304)
    c: InternalAlignment(g305,g304)
    c: InternalAlignment(g306,g304)
    c: Block(g304)
    c: Block(g298)
    c: Block(g292)
    c: Coincident(g307,g298)
    c: Coincident(g307,g292)
    c: Coincident(g308,g292)
    c: Coincident(g308,g304)
    c: Vertical(g308)
    c: Coincident(g309,g304)
    c: Coincident(g309,g298)
    c: Horizontal(g309)
    c: Horizontal(g310)
    c: Horizontal(g313)
    c: Horizontal(g314)
    c: Vertical(g315)
    c: Vertical(g316)
    c: Horizontal(g317)
FEATURE [Sketcher::SketchObject] Sketch001
  FullyConstrained = true
  MapMode = 4
  Placement = pos=(0,0,0) rot=(0.57735,0.57735,0.57735;2.0944rad)
  Support = -> [Sketch]
  sketch-geometry (46):
    g0: BSplineCurve PolesCount=3 KnotsCount=2 Degree=2 IsPeriodic=0
    g1: ArcOfCircle CenterX=73.1223 CenterY=-32.291 CenterZ=0 NormalX=0 NormalY=0 NormalZ=1 AngleXU=0 Radius=13 StartAngle=5.92268 EndAngle=9.06428
    g2: ArcOfCircle CenterX=66.7816 CenterY=-49.1439 CenterZ=0 NormalX=0 NormalY=0 NormalZ=1 AngleXU=0 Radius=13 StartAngle=2.78068 EndAngle=5.92131
    g3: ArcOfCircle CenterX=55.9263 CenterY=-78.1807 CenterZ=0 NormalX=0 NormalY=0 NormalZ=1 AngleXU=0 Radius=13 StartAngle=5.92268 EndAngle=9.06428
    g4: ArcOfCircle CenterX=49.5884 CenterY=-95.0342 CenterZ=0 NormalX=0 NormalY=0 NormalZ=1 AngleXU=0 Radius=13 StartAngle=2.78068 EndAngle=5.92131
    g5: ArcOfCircle CenterX=38.7206 CenterY=-124.067 CenterZ=0 NormalX=0 NormalY=0 NormalZ=1 AngleXU=0 Radius=13 StartAngle=5.92268 EndAngle=9.06428
    g6: ArcOfCircle CenterX=32.3875 CenterY=-140.92 CenterZ=0 NormalX=0 NormalY=0 NormalZ=1 AngleXU=0 Radius=13 StartAngle=2.78068 EndAngle=5.92131
    g7: ArcOfCircle CenterX=21.4715 CenterY=-169.934 CenterZ=0 NormalX=0 NormalY=0 NormalZ=1 AngleXU=0 Radius=13 StartAngle=5.92268 EndAngle=9.06428
    g8: ArcOfCircle CenterX=15.1336 CenterY=-186.787 CenterZ=0 NormalX=0 NormalY=0 NormalZ=1 AngleXU=0 Radius=13 StartAngle=2.78068 EndAngle=5.92131
    g9-g12: Circle x4 (B-spline internal-alignment scaffolding for g13; pole/knot coordinates omitted)
    g13: BSplineCurve PolesCount=4 KnotsCount=2 Degree=3 IsPeriodic=0
    g14: GeomPoint X=28.8094 Y=-19.0875 Z=0
    g15: GeomPoint X=47.0443 Y=-50.4712 Z=0
    g16: Circle CenterX=53.5586 CenterY=-23.2695 CenterZ=0 NormalX=0 NormalY=0 NormalZ=1 AngleXU=0 Radius=3.24518
    g17: Circle CenterX=-195.441 CenterY=-127.082 CenterZ=0 NormalX=0 NormalY=0 NormalZ=1 AngleXU=0 Radius=1
    g18: Circle CenterX=-8.24091 CenterY=-197.481 CenterZ=0 NormalX=0 NormalY=0 NormalZ=1 AngleXU=0 Radius=1
    g19: Circle CenterX=12.8789 CenterY=-141.321 CenterZ=0 NormalX=0 NormalY=0 NormalZ=1 AngleXU=0 Radius=1
    g20: BSplineCurve PolesCount=3 KnotsCount=2 Degree=2 IsPeriodic=0
    g21: GeomPoint X=-195.441 Y=-127.082 Z=0
    g22: GeomPoint X=12.8789 Y=-141.321 Z=0
    g23: Circle CenterX=-12.8016 CenterY=-179.036 CenterZ=0 NormalX=0 NormalY=0 NormalZ=1 AngleXU=0 Radius=10.5072
    g24: Circle CenterX=0.933922 CenterY=-166.43 CenterZ=0 NormalX=0 NormalY=0 NormalZ=1 AngleXU=0 Radius=3.26661
    g25: Circle CenterX=-33.5518 CenterY=-176.44 CenterZ=0 NormalX=0 NormalY=0 NormalZ=1 AngleXU=0 Radius=5.64388
    g26: Circle CenterX=-47.2366 CenterY=-173.859 CenterZ=0 NormalX=0 NormalY=0 NormalZ=1 AngleXU=0 Radius=3.01653
    g27: Circle CenterX=-56.2595 CenterY=-171.456 CenterZ=0 NormalX=0 NormalY=0 NormalZ=1 AngleXU=0 Radius=2.12826
    g28: ArcOfCircle CenterX=51.2151 CenterY=-198.473 CenterZ=0 NormalX=0 NormalY=0 NormalZ=1 AngleXU=0 Radius=20 StartAngle=2.78189 EndAngle=4.35269
    g29: LineSegment StartX=32.4951 StartY=-191.433 StartZ=0 EndX=94.6578 EndY=-26.1352 EndZ=0
    g30: LineSegment StartX=43.1192 StartY=-220.001 StartZ=0 EndX=-196.497 EndY=-129.89 EndZ=0
    g31: LineSegment StartX=43.1192 StartY=-220.001 StartZ=0 EndX=44.1752 EndY=-217.193 EndZ=0
    g32: LineSegment StartX=117.223 StartY=-19.0875 StartZ=0 EndX=117.223 EndY=-16.0875 EndZ=0
    g33: LineSegment StartX=117.223 StartY=-16.0875 StartZ=0 EndX=17.2232 EndY=-16.0875 EndZ=0
    g34: LineSegment StartX=17.2232 StartY=-16.0875 StartZ=0 EndX=17.2232 EndY=-19.0875 EndZ=0
    g35: LineSegment StartX=28.8094 StartY=-19.0875 StartZ=0 EndX=17.2232 EndY=-19.0875 EndZ=0
    g36: LineSegment StartX=47.0443 StartY=-50.4712 StartZ=0 EndX=12.8789 EndY=-141.321 EndZ=0
    g37: LineSegment StartX=-195.441 StartY=-127.082 StartZ=0 EndX=-196.497 EndY=-129.89 EndZ=0
    g38: LineSegment StartX=85.2866 StartY=-36.8766 StartZ=0 EndX=78.9396 EndY=-53.7463 EndZ=0
    g39: LineSegment StartX=60.9579 StartY=-27.7053 StartZ=0 EndX=54.6191 EndY=-44.5532 EndZ=0
    g40: LineSegment StartX=68.0907 StartY=-82.7664 StartZ=0 EndX=61.7465 EndY=-99.6365 EndZ=0
    g41: LineSegment StartX=43.7619 StartY=-73.595 StartZ=0 EndX=37.426 EndY=-90.4435 EndZ=0
    g42: LineSegment StartX=50.885 StartY=-128.652 StartZ=0 EndX=44.5456 EndY=-145.522 EndZ=0
    g43: LineSegment StartX=26.5562 StartY=-119.481 StartZ=0 EndX=20.2251 EndY=-136.329 EndZ=0
    g44: LineSegment StartX=9.3071 StartY=-165.349 StartZ=0 EndX=2.97115 EndY=-182.197 EndZ=0
    g45: LineSegment StartX=33.6358 StartY=-174.52 StartZ=0 EndX=27.2917 EndY=-191.39 EndZ=0
  constraints (71):
    c: Block(g0)
    c: Block(g1)
    c: Block(g2)
    c: Block(g4)
    c: Block(g3)
    c: Block(g6)
    c: Block(g5)
    c: Block(g8)
    c: Block(g7)
    c: Weight(g9) = 1
    c: Equal(g9,g10)
    c: Equal(g9,g11)
    c: Equal(g9,g12)
    c: InternalAlignment(g9-g12 -> g13) x4
    c: InternalAlignment(g14,g13)
    c: InternalAlignment(g15,g13)
    c: Block(g16)
    c: Weight(g17) = 1
    c: Equal(g17,g18)
    c: Equal(g17,g19)
    c: InternalAlignment(g17,g20)
    c: InternalAlignment(g18,g20)
    c: InternalAlignment(g19,g20)
    c: InternalAlignment(g21,g20)
    c: InternalAlignment(g22,g20)
    c: Block(g20)
    c: Block(g23)
    c: Block(g24)
    c: Block(g25)
    c: Block(g26)
    c: Block(g27)
    c: Block(g28)
    c: Coincident(g29,g28)
    c: Coincident(g29,g0)
    c: Block(g13)
    c: Coincident(g31,g30)
    c: Coincident(g31,g28)
    c: Block(g31)
    c: Coincident(g32,g0)
    c: Vertical(g32)
    c: Coincident(g33,g32)
    c: Horizontal(g33)
    c: Coincident(g34,g33)
    c: Vertical(g34)
    c: Block(g33)
    c: Coincident(g35,g13)
    c: Coincident(g35,g34)
    c: Horizontal(g35)
    c: Coincident(g36,g13)
    c: Coincident(g36,g20)
    c: Coincident(g37,g20)
    c: Coincident(g37,g30)
    c: Block(g30)
    c: Coincident(g38,g1)
    c: Coincident(g38,g2)
    c: Coincident(g39,g1)
    c: Coincident(g39,g2)
    c: Coincident(g40,g3)
    c: Coincident(g40,g4)
    c: Coincident(g41,g3)
    c: Coincident(g41,g4)
    c: Coincident(g42,g5)
    c: Coincident(g42,g6)
    c: Coincident(g43,g5)
    c: Coincident(g43,g6)
    c: Coincident(g44,g7)
    c: Coincident(g44,g8)
    c: Coincident(g45,g7)
    c: Coincident(g45,g8)
    c: Distance(g30) = 256
    c: Distance(g33) = 100
FEATURE [Part::Extrusion] Extrude002
  Base = -> Sketch001
  Dir = (1,0,0)
  DirMode = 2
  FaceMakerClass = Part::FaceMakerBullseye
  LengthFwd = 8
  LengthRev = 0
  Solid = true
  Symmetric = false
FEATURE [Sketcher::SketchObject] Sketch002
  FullyConstrained = true
  sketch-geometry (20):
    g0: LineSegment StartX=-2.77179 StartY=-200.304 StartZ=0 EndX=5.22821 EndY=-200.304 EndZ=0
    g1: LineSegment StartX=5.22821 StartY=-200.304 StartZ=0 EndX=5.22821 EndY=-197.304 EndZ=0
    g2: LineSegment StartX=-2.77179 StartY=-200.304 StartZ=0 EndX=-2.77179 EndY=-197.304 EndZ=0
    g3: LineSegment StartX=5.22821 StartY=-197.304 StartZ=0 EndX=8.22821 EndY=-197.304 EndZ=0
    g4: LineSegment StartX=-2.77179 StartY=-197.304 StartZ=0 EndX=-5.77179 EndY=-197.304 EndZ=0
    g5: LineSegment StartX=19.2282 StartY=-203.304 StartZ=0 EndX=19.2282 EndY=-206.304 EndZ=0
    g6: LineSegment StartX=-16.7718 StartY=-203.304 StartZ=0 EndX=-16.7718 EndY=-206.304 EndZ=0
    g7: LineSegment StartX=-16.7718 StartY=-206.304 StartZ=0 EndX=19.2282 EndY=-206.304 EndZ=0
    g8: Circle CenterX=-16.7718 CenterY=-203.304 CenterZ=0 NormalX=0 NormalY=0 NormalZ=1 AngleXU=0 Radius=1
    g9: Circle CenterX=-5.77179 CenterY=-203.304 CenterZ=0 NormalX=0 NormalY=0 NormalZ=1 AngleXU=0 Radius=1
    g10: Circle CenterX=-5.77179 CenterY=-197.304 CenterZ=0 NormalX=0 NormalY=0 NormalZ=1 AngleXU=0 Radius=1
    g11: BSplineCurve PolesCount=3 KnotsCount=2 Degree=2 IsPeriodic=0
    g12: GeomPoint X=-16.7718 Y=-203.304 Z=0
    g13: GeomPoint X=-5.77179 Y=-197.304 Z=0
    g14: Circle CenterX=19.2282 CenterY=-203.304 CenterZ=0 NormalX=0 NormalY=0 NormalZ=1 AngleXU=0 Radius=1
    g15: Circle CenterX=8.22821 CenterY=-203.304 CenterZ=0 NormalX=0 NormalY=0 NormalZ=1 AngleXU=0 Radius=1
    g16: Circle CenterX=8.22821 CenterY=-197.304 CenterZ=0 NormalX=0 NormalY=0 NormalZ=1 AngleXU=0 Radius=1
    g17: BSplineCurve PolesCount=3 KnotsCount=2 Degree=2 IsPeriodic=0
    g18: GeomPoint X=19.2282 Y=-203.304 Z=0
    g19: GeomPoint X=8.22821 Y=-197.304 Z=0
  constraints (41):
    c: Horizontal(g0)
    c: Distance(g0) = 8
    c: Coincident(g1,g0)
    c: Vertical(g1)
    c: Distance(g1) = 3
    c: Coincident(g2,g0)
    c: Vertical(g2)
    c: Distance(g2) = 3
    c: Coincident(g3,g1)
    c: Horizontal(g3)
    c: Distance(g3) = 3
    c: Coincident(g4,g2)
    c: Horizontal(g4)
    c: Distance(g4) = 3
    c: Vertical(g5)
    c: Vertical(g6)
    c: Coincident(g7,g6)
    c: Coincident(g7,g5)
    c: Weight(g8) = 1
    c: Equal(g8,g9)
    c: Equal(g8,g10)
    c: Coincident(g11,g4)
    c: InternalAlignment(g8,g11)
    c: InternalAlignment(g9,g11)
    c: InternalAlignment(g10,g11)
    c: InternalAlignment(g12,g11)
    c: InternalAlignment(g13,g11)
    c: Coincident(g17,g5)
    c: Weight(g14) = 1
    c: Equal(g14,g15)
    c: Equal(g14,g16)
    c: Coincident(g17,g3)
    c: InternalAlignment(g14,g17)
    c: InternalAlignment(g15,g17)
    c: InternalAlignment(g16,g17)
    c: InternalAlignment(g18,g17)
    c: InternalAlignment(g19,g17)
    c: Block(g7)
    c: Block(g17)
    c: Block(g11)
    c: Block(g6)
FEATURE [Part::Extrusion] Extrude003
  Base = -> Sketch002
  Dir = (0,0,1)
  DirMode = 2
  FaceMakerClass = Part::FaceMakerBullseye
  LengthFwd = 260
  LengthRev = 0
  Solid = true
  Symmetric = false
FEATURE [Part::Extrusion] Extrude
  Base = -> Sketch
  Dir = (0,0,1)
  DirMode = 2
  FaceMakerClass = Part::FaceMakerBullseye
  LengthFwd = 14
  LengthRev = 0
  Solid = true
  Symmetric = false
